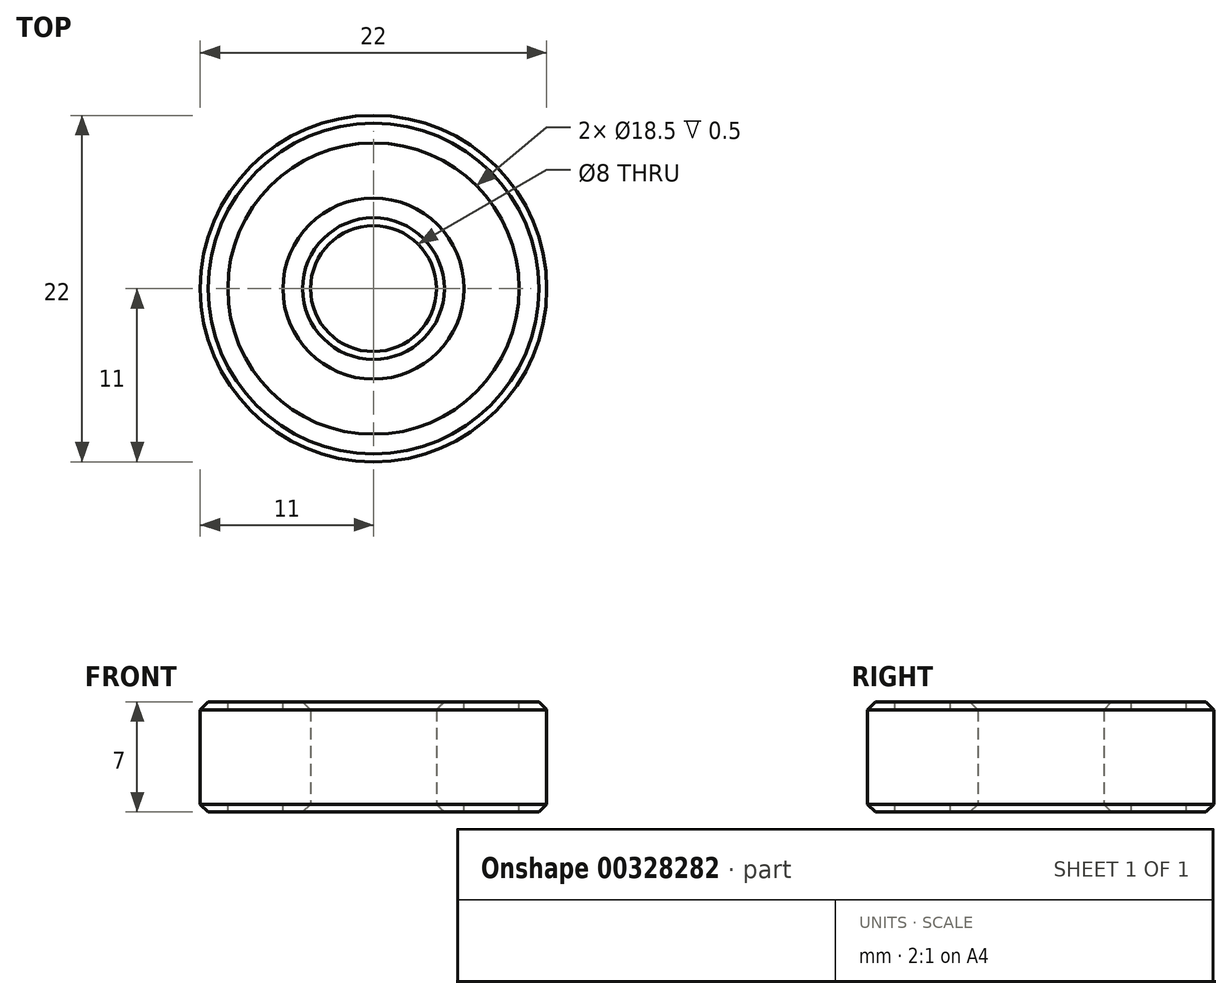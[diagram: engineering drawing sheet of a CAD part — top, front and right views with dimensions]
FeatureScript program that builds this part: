
annotation { "Feature Type Name" : "Feature", "Feature Type Description" : "" }
export const myFeature = defineFeature(function(context is Context, id is Id, definition is map)
    precondition{}
    {
        {
            var Q0;
            Q0=qCreatedBy(makeId("Top.planeOp"),FACE);
            var sketch = newSketch(context, id + "F0", { "sketchPlane" : qUnion([Q0])});
            skCircle(sketch, "E0", {"center": v(0, 0) * mm, "radius": 4 * mm});
            skCircle(sketch, "E1", {"center": v(0, 0) * mm, "radius": 11 * mm});
            skSolve(sketch);
        }
        {
            var Q0;
            Q0=makeQuery(id+"F0.imprint","IMPRINT",FACE,{"disambiguationData":[TD([[makeQuery(id+"F0.imprint","IMPRINT",EDGE,{"derivedFrom":sQuery(id+"F0.wireOp",EDGE,"E0")}),-1.0]])]});
            extrude(context, id + "F1", {"entities" : qUnion([Q0]), "depth" : 7 * mm, "symmetric" : true});
        }
        {
            var Q0;
            Q0=makeQuery(id+"F1.opExtrude","CAP_EDGE",EDGE,{"disambiguationData":[OSD([sQuery(id+"F0.wireOp",EDGE,"E1")])],"isStart":false});
            var Q1;
            Q1=makeQuery(id+"F1.opExtrude","CAP_EDGE",EDGE,{"disambiguationData":[OSD([sQuery(id+"F0.wireOp",EDGE,"E1")])],"isStart":true});
            var Q2;
            Q2=makeQuery(id+"F1.opExtrude","CAP_EDGE",EDGE,{"disambiguationData":[OSD([sQuery(id+"F0.wireOp",EDGE,"E0")])],"isStart":false});
            var Q3;
            Q3=makeQuery(id+"F1.opExtrude","CAP_EDGE",EDGE,{"disambiguationData":[OSD([sQuery(id+"F0.wireOp",EDGE,"E0")])],"isStart":true});
            chamfer(context, id + "F2", {"entities" : qUnion([Q0, Q1, Q2, Q3]), "width" : 0.5 * mm, "tangentPropagation" : true});
        }
        {
            var Q0;
            Q0=qCreatedBy(makeId("Right.planeOp"),FACE);
            var sketch = newSketch(context, id + "F3", { "sketchPlane" : qUnion([Q0])});
            skLineSegment(sketch, "E2.0", {"start": v(4.5, 3.5) * mm, "end": v(10.5, 3.5) * mm});
            skPoint(sketch, "E3.0.end.orphan", {"position": v(-4.5, 3.5) * mm});
            skPoint(sketch, "E3.0.start.orphan", {"position": v(4.5, 3.5) * mm});
            skPoint(sketch, "E4.orphan", {"position": v(-10.5, 3.5) * mm});
            skPoint(sketch, "E5.0.end.orphan", {"position": v(-10.5, -3.5) * mm});
            skPoint(sketch, "E5.0.start.orphan", {"position": v(10.5, -3.5) * mm});
            skLineSegment(sketch, "E6.bottom", {"start": v(5.75, 3) * mm, "end": v(9.25, 3) * mm});
            skLineSegment(sketch, "E6.top", {"start": v(5.75, 4) * mm, "end": v(9.25, 4) * mm});
            skLineSegment(sketch, "E6.left", {"start": v(5.75, 3) * mm, "end": v(5.75, 4) * mm});
            skLineSegment(sketch, "E6.right", {"start": v(9.25, 3) * mm, "end": v(9.25, 4) * mm});
            skPoint(sketch, "E6.middle", {"position": v(7.5, 3.5) * mm});
            skLineSegment(sketch, "E7", {"start": v(11, 3) * mm, "end": v(11, -3) * mm});
            skLineSegment(sketch, "E8.MirrorCS", {"start": v(5.75, -4) * mm, "end": v(9.25, -4) * mm});
            skLineSegment(sketch, "E9.MirrorCS", {"start": v(5.75, -3) * mm, "end": v(9.25, -3) * mm});
            skLineSegment(sketch, "E10.MirrorCS", {"start": v(5.75, -3) * mm, "end": v(5.75, -4) * mm});
            skLineSegment(sketch, "E11.MirrorCS", {"start": v(9.25, -3) * mm, "end": v(9.25, -4) * mm});
            skPoint(sketch, "E12.MirrorP", {"position": v(7.5, -3.5) * mm});
            skSolve(sketch);
        }
        {
            var Q0;
            Q0 = qSketchRegion(id + "F3", true);
            var Q1;
            {var subQ0=sQuery(id+"F0.wireOp",EDGE,"E0");Q1=makeQuery(id+"F2.opChamfer","BLEND_EDGE",EDGE,{"blendedFrom":[makeQuery(id+"F1.opExtrude","CAP_EDGE",EDGE,{"disambiguationData":[OSD([subQ0])],"isStart":false}),makeQuery(id+"F1.opExtrude","CAP_FACE",FACE,{"disambiguationData":[OSD([subQ0,sQuery(id+"F0.wireOp",EDGE,"E1")])],"isStart":false})],"blendedInto":[makeQuery(id+"F1.opExtrude","CAP_FACE",FACE,{"disambiguationData":[OSD([subQ0,sQuery(id+"F0.wireOp",EDGE,"E1")])],"isStart":false})]});}
            revolve(context, id + "F4", {"operationType" : NewBodyOperationType.REMOVE, "entities" : qUnion([Q0]), "axis" : qUnion([Q1]), "revolveType" : RevolveType.FULL, "oppositeDirection" : true});
        }
    });
